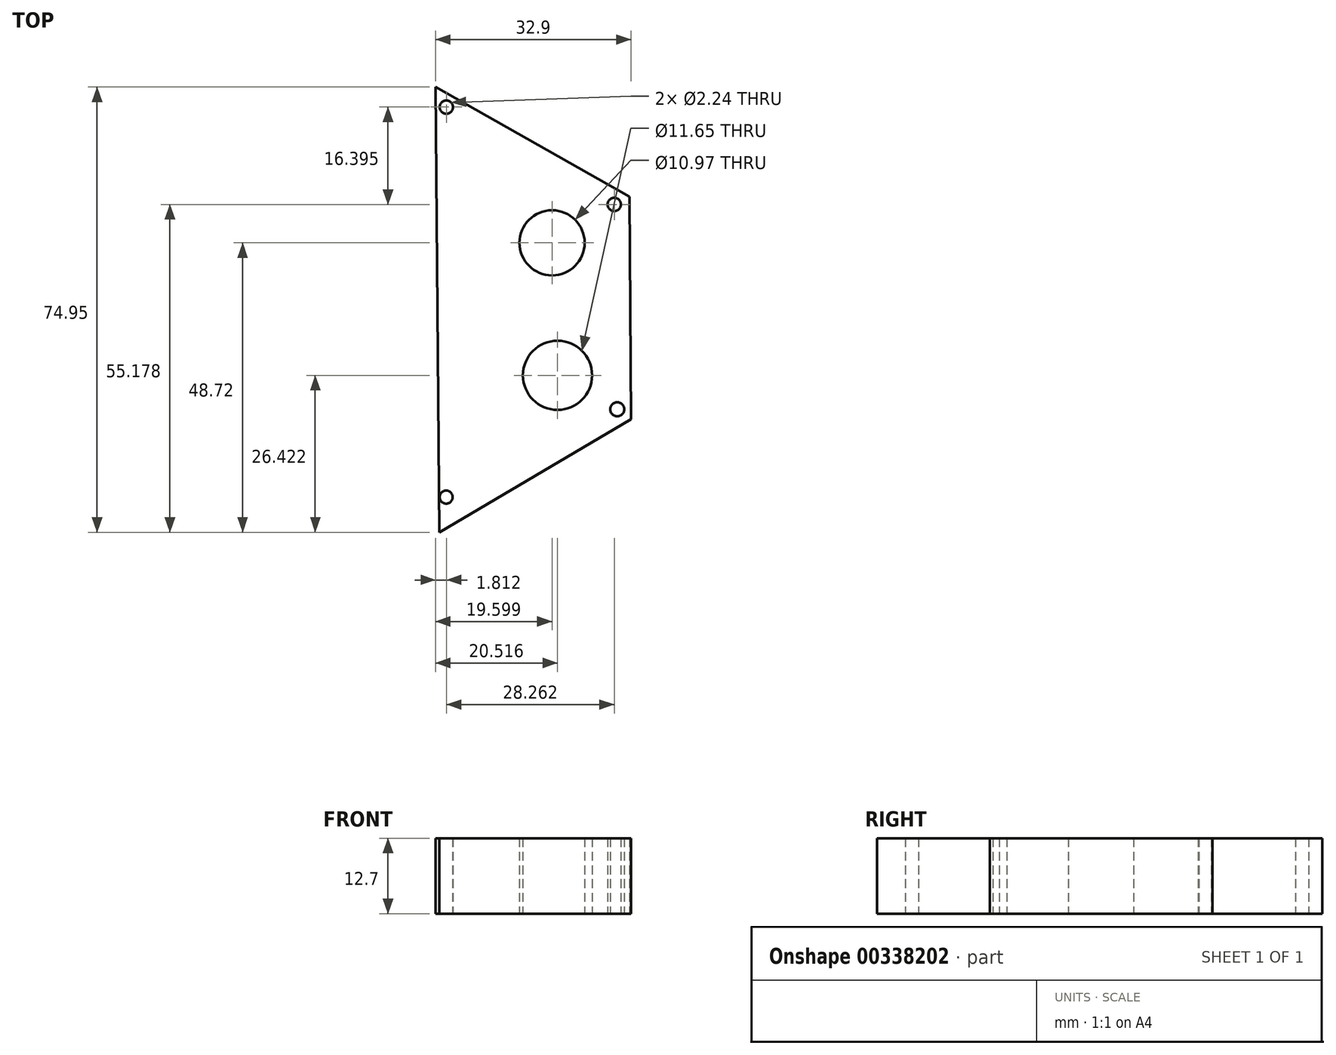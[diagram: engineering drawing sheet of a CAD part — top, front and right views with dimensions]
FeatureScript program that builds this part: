
annotation { "Feature Type Name" : "Feature", "Feature Type Description" : "" }
export const myFeature = defineFeature(function(context is Context, id is Id, definition is map)
    precondition{}
    {
        {
            var Q0;
            Q0=qCreatedBy(makeId("Top.planeOp"),FACE);
            var sketch = newSketch(context, id + "F0", { "sketchPlane" : qUnion([Q0])});
            skLineSegment(sketch, "E0.0", {"start": v(-39.75, 46.8) * mm, "end": v(-7.15, 28.33) * mm});
            skLineSegment(sketch, "E0.1", {"start": v(-7.15, 28.33) * mm, "end": v(-6.85, -9.14) * mm});
            skLineSegment(sketch, "E0.2", {"start": v(-6.85, -9.14) * mm, "end": v(-39.15, -28.14) * mm});
            skPoint(sketch, "E0.0.midPoint", {"position": v(-23.45, 37.57) * mm});
            skLineSegment(sketch, "E1", {"start": v(-39.15, -28.14) * mm, "end": v(-39.75, 46.8) * mm});
            skPoint(sketch, "E2.orphan", {"position": v(-72.05, 27.81) * mm});
            skPoint(sketch, "E3.end.orphan", {"position": v(-39.67, 37.57) * mm});
            skCircle(sketch, "E4", {"center": v(-20.15, 20.58) * mm, "radius": 5.48 * mm});
            skCircle(sketch, "E5", {"center": v(-19.23, -1.72) * mm, "radius": 5.82 * mm});
            skCircle(sketch, "E6", {"center": v(-9.68, 27.04) * mm, "radius": 1.12 * mm});
            skCircle(sketch, "E7", {"center": v(-9.18, -7.44) * mm, "radius": 1.18 * mm});
            skCircle(sketch, "E8", {"center": v(-37.97, -22.22) * mm, "radius": 1.1 * mm});
            skCircle(sketch, "E9", {"center": v(-37.94, 43.43) * mm, "radius": 1.12 * mm});
            skSolve(sketch);
        }
        {
            var Q0;
            Q0=makeQuery(id+"F0.imprint","IMPRINT",FACE,{"disambiguationData":[TD([[makeQuery(id+"F0.imprint","IMPRINT",EDGE,{"derivedFrom":sQuery(id+"F0.wireOp",EDGE,"E0.1")}),-1.0]])]});
            extrude(context, id + "F1", {"entities" : qUnion([Q0]), "depth" : 12.7 * mm});
        }
    });
